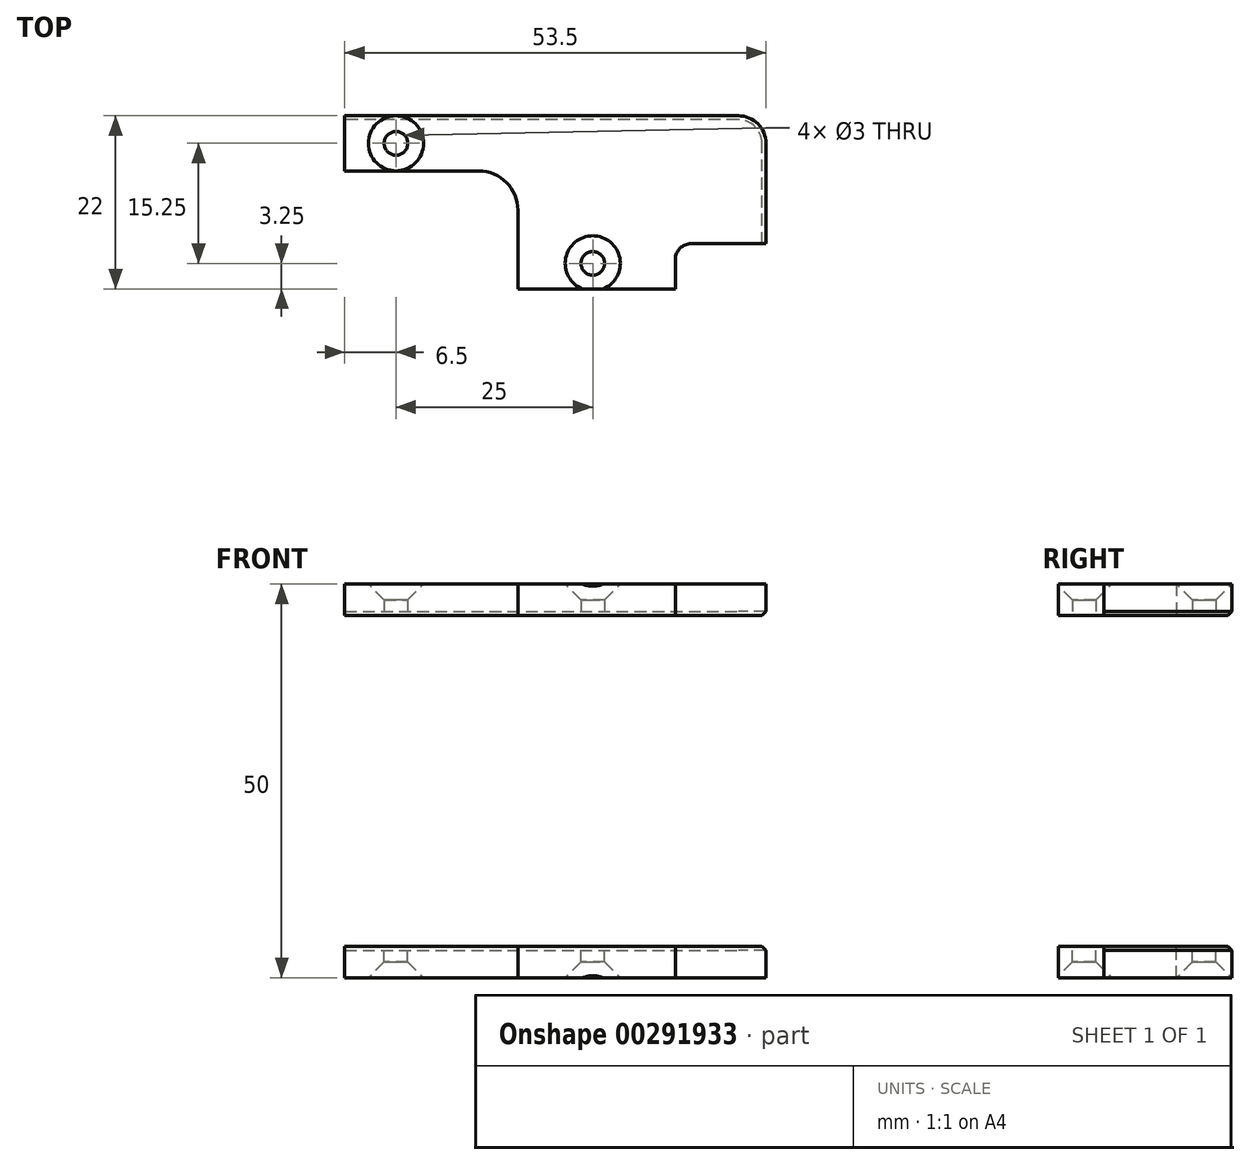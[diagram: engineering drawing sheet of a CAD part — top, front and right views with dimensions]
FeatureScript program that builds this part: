
annotation { "Feature Type Name" : "Feature", "Feature Type Description" : "" }
export const myFeature = defineFeature(function(context is Context, id is Id, definition is map)
    precondition{}
    {
        {
            var Q0;
            Q0=qCreatedBy(makeId("Top.planeOp"),FACE);
            var sketch = newSketch(context, id + "F0", { "sketchPlane" : qUnion([Q0])});
            skLineSegment(sketch, "E0.bottom", {"start": v(0, 0) * mm, "end": v(42, 0) * mm});
            skLineSegment(sketch, "E0.top", {"start": v(0, -22) * mm, "end": v(42, -22) * mm});
            skLineSegment(sketch, "E0.left", {"start": v(0, 0) * mm, "end": v(0, -22) * mm});
            skLineSegment(sketch, "E0.right", {"start": v(42, 0) * mm, "end": v(42, -22) * mm});
            skSolve(sketch);
        }
        {
            var Q0;
            Q0=makeQuery(id+"F0.imprint","IMPRINT",FACE,{"disambiguationData":[TD([[makeQuery(id+"F0.imprint","IMPRINT",EDGE,{"derivedFrom":sQuery(id+"F0.wireOp",EDGE,"E0.bottom")}),-1.0]])]});
            extrude(context, id + "F1", {"entities" : qUnion([Q0]), "depth" : 4 * mm});
        }
        {
            var Q0;
            Q0=qCreatedBy(makeId("Top.planeOp"),FACE);
            var sketch = newSketch(context, id + "F2", { "sketchPlane" : qUnion([Q0])});
            skLineSegment(sketch, "E1.bottom", {"start": v(24.5, 0) * mm, "end": v(53.5, 0) * mm});
            skLineSegment(sketch, "E1.top", {"start": v(24.5, -16.25) * mm, "end": v(53.5, -16.25) * mm});
            skLineSegment(sketch, "E1.left", {"start": v(24.5, 0) * mm, "end": v(24.5, -16.25) * mm});
            skLineSegment(sketch, "E1.right", {"start": v(53.5, 0) * mm, "end": v(53.5, -16.25) * mm});
            skSolve(sketch);
        }
        {
            var Q0;
            Q0=makeQuery(id+"F2.imprint","IMPRINT",FACE,{"disambiguationData":[TD([[makeQuery(id+"F2.imprint","IMPRINT",EDGE,{"derivedFrom":sQuery(id+"F2.wireOp",EDGE,"E1.bottom")}),-1.0]])]});
            extrude(context, id + "F3", {"entities" : qUnion([Q0]), "operationType" : NewBodyOperationType.ADD, "depth" : 4 * mm});
        }
        {
            var Q0;
            Q0=makeQuery(id+"F3.opExtrude","SWEPT_EDGE",EDGE,{"disambiguationData":[OSD([sQuery(id+"F2.wireOp",EDGE,"E1.bottom"),sQuery(id+"F2.wireOp",EDGE,"E1.right")])]});
            fillet(context, id + "F4", {"entities" : qUnion([Q0]), "radius" : 3.5 * mm, "tangentPropagation" : true, "allowEdgeOverflow" : false});
        }
        {
            var Q0;
            Q0=makeQuery(id+"F3.boolean.opBoolean","INTERSECT",EDGE,{"derivedFrom":[makeQuery(id+"F1.opExtrude","SWEPT_FACE",FACE,{"disambiguationData":[OSD([sQuery(id+"F0.wireOp",EDGE,"E0.right")])]}),makeQuery(id+"F3.opExtrude","SWEPT_FACE",FACE,{"disambiguationData":[OSD([sQuery(id+"F2.wireOp",EDGE,"E1.top")])]})]});
            fillet(context, id + "F5", {"entities" : qUnion([Q0]), "radius" : 2 * mm, "tangentPropagation" : true, "allowEdgeOverflow" : false});
        }
        {
            var Q0;
            Q0=makeQuery(id+"F3.boolean.opBoolean","MERGE",FACE,{"derivedFrom":[makeQuery(id+"F1.opExtrude","CAP_FACE",FACE,{"disambiguationData":[OSD([sQuery(id+"F0.wireOp",EDGE,"E0.bottom"),sQuery(id+"F0.wireOp",EDGE,"E0.top"),sQuery(id+"F0.wireOp",EDGE,"E0.left"),sQuery(id+"F0.wireOp",EDGE,"E0.right")])],"isStart":false}),makeQuery(id+"F3.opExtrude","CAP_FACE",FACE,{"disambiguationData":[OSD([sQuery(id+"F2.wireOp",EDGE,"E1.bottom"),sQuery(id+"F2.wireOp",EDGE,"E1.top"),sQuery(id+"F2.wireOp",EDGE,"E1.left"),sQuery(id+"F2.wireOp",EDGE,"E1.right")])],"isStart":false})]});
            var sketch = newSketch(context, id + "F6", { "sketchPlane" : qUnion([Q0])});
            skCircle(sketch, "E2", {"center": v(6.5, -3.5) * mm, "radius": 1.5 * mm});
            skSolve(sketch);
        }
        {
            var Q0;
            Q0=makeQuery(id+"F6.imprint","IMPRINT",FACE,{"disambiguationData":[TD([[makeQuery(id+"F6.imprint","IMPRINT",EDGE,{"derivedFrom":sQuery(id+"F6.wireOp",EDGE,"E2")}),1.0]])]});
            extrude(context, id + "F7", {"entities" : qUnion([Q0]), "operationType" : NewBodyOperationType.REMOVE, "oppositeDirection" : true, "depth" : 25 * mm});
        }
        {
            var Q0;
            Q0=makeQuery(id+"F3.boolean.opBoolean","MERGE",FACE,{"derivedFrom":[makeQuery(id+"F1.opExtrude","CAP_FACE",FACE,{"disambiguationData":[OSD([sQuery(id+"F0.wireOp",EDGE,"E0.bottom"),sQuery(id+"F0.wireOp",EDGE,"E0.top"),sQuery(id+"F0.wireOp",EDGE,"E0.left"),sQuery(id+"F0.wireOp",EDGE,"E0.right")])],"isStart":false}),makeQuery(id+"F3.opExtrude","CAP_FACE",FACE,{"disambiguationData":[OSD([sQuery(id+"F2.wireOp",EDGE,"E1.bottom"),sQuery(id+"F2.wireOp",EDGE,"E1.top"),sQuery(id+"F2.wireOp",EDGE,"E1.left"),sQuery(id+"F2.wireOp",EDGE,"E1.right")])],"isStart":false})]});
            var sketch = newSketch(context, id + "F8", { "sketchPlane" : qUnion([Q0])});
            skLineSegment(sketch, "E3.bottom", {"start": v(0, -22) * mm, "end": v(22, -22) * mm});
            skLineSegment(sketch, "E3.top", {"start": v(0, -7) * mm, "end": v(22, -7) * mm});
            skLineSegment(sketch, "E3.left", {"start": v(0, -22) * mm, "end": v(0, -7) * mm});
            skLineSegment(sketch, "E3.right", {"start": v(22, -22) * mm, "end": v(22, -7) * mm});
            skSolve(sketch);
        }
        {
            var Q0;
            Q0=makeQuery(id+"F8.imprint","IMPRINT",FACE,{"disambiguationData":[TD([[makeQuery(id+"F8.imprint","IMPRINT",EDGE,{"derivedFrom":sQuery(id+"F8.wireOp",EDGE,"E3.bottom")}),1.0]])]});
            extrude(context, id + "F9", {"entities" : qUnion([Q0]), "operationType" : NewBodyOperationType.REMOVE, "oppositeDirection" : true, "depth" : 25 * mm});
        }
        {
            var Q0;
            Q0=makeQuery(id+"F9.boolean.opBoolean","COPY",EDGE,{"derivedFrom":makeQuery(id+"F9.opExtrude","SWEPT_EDGE",EDGE,{"disambiguationData":[OSD([sQuery(id+"F8.wireOp",EDGE,"E3.top"),sQuery(id+"F8.wireOp",EDGE,"E3.right")])]})});
            fillet(context, id + "F10", {"entities" : qUnion([Q0]), "radius" : 5 * mm, "tangentPropagation" : true, "allowEdgeOverflow" : false});
        }
        {
            var Q0;
            Q0=makeQuery(id+"F3.boolean.opBoolean","MERGE",FACE,{"derivedFrom":[makeQuery(id+"F1.opExtrude","CAP_FACE",FACE,{"disambiguationData":[OSD([sQuery(id+"F0.wireOp",EDGE,"E0.bottom"),sQuery(id+"F0.wireOp",EDGE,"E0.top"),sQuery(id+"F0.wireOp",EDGE,"E0.left"),sQuery(id+"F0.wireOp",EDGE,"E0.right")])],"isStart":false}),makeQuery(id+"F3.opExtrude","CAP_FACE",FACE,{"disambiguationData":[OSD([sQuery(id+"F2.wireOp",EDGE,"E1.bottom"),sQuery(id+"F2.wireOp",EDGE,"E1.top"),sQuery(id+"F2.wireOp",EDGE,"E1.left"),sQuery(id+"F2.wireOp",EDGE,"E1.right")])],"isStart":false})]});
            var sketch = newSketch(context, id + "F11", { "sketchPlane" : qUnion([Q0])});
            skCircle(sketch, "E4", {"center": v(31.5, -18.75) * mm, "radius": 1.5 * mm});
            skSolve(sketch);
        }
        {
            var Q0;
            Q0=qSketchRegion(id+"F11",true);
            var Q1;
            Q1=sQuery(id+"F11.wireOp",EDGE,"E4");
            extrude(context, id + "F12", {"entities" : qUnion([Q0]), "operationType" : NewBodyOperationType.REMOVE, "surfaceEntities" : qUnion([Q1]), "oppositeDirection" : true, "depth" : 25 * mm});
        }
        {
            var Q0;
            Q0=qCreatedBy(makeId("Top.planeOp"),FACE);
            cPlane(context, id + "F13", {"entities" : qUnion([Q0]), "cplaneType" : CPlaneType.OFFSET, "offset" : 25 * mm, "width" : 150 * mm, "height" : 150 * mm});
        }
        {
            var Q0;
            Q0=makeQuery(id+"F12.boolean.opBoolean","INTERSECT",EDGE,{"derivedFrom":[makeQuery(id+"F3.boolean.opBoolean","MERGE",FACE,{"derivedFrom":[makeQuery(id+"F1.opExtrude","CAP_FACE",FACE,{"disambiguationData":[OSD([sQuery(id+"F0.wireOp",EDGE,"E0.bottom"),sQuery(id+"F0.wireOp",EDGE,"E0.top"),sQuery(id+"F0.wireOp",EDGE,"E0.left"),sQuery(id+"F0.wireOp",EDGE,"E0.right")])],"isStart":true}),makeQuery(id+"F3.opExtrude","CAP_FACE",FACE,{"disambiguationData":[OSD([sQuery(id+"F2.wireOp",EDGE,"E1.bottom"),sQuery(id+"F2.wireOp",EDGE,"E1.top"),sQuery(id+"F2.wireOp",EDGE,"E1.left"),sQuery(id+"F2.wireOp",EDGE,"E1.right")])],"isStart":true})]}),makeQuery(id+"F12.opExtrude","SWEPT_FACE",FACE,{"disambiguationData":[OSD([sQuery(id+"F11.wireOp",EDGE,"E4")])]})]});
            var Q1;
            Q1=makeQuery(id+"F7.boolean.opBoolean","INTERSECT",EDGE,{"derivedFrom":[makeQuery(id+"F3.boolean.opBoolean","MERGE",FACE,{"derivedFrom":[makeQuery(id+"F1.opExtrude","CAP_FACE",FACE,{"disambiguationData":[OSD([sQuery(id+"F0.wireOp",EDGE,"E0.bottom"),sQuery(id+"F0.wireOp",EDGE,"E0.top"),sQuery(id+"F0.wireOp",EDGE,"E0.left"),sQuery(id+"F0.wireOp",EDGE,"E0.right")])],"isStart":true}),makeQuery(id+"F3.opExtrude","CAP_FACE",FACE,{"disambiguationData":[OSD([sQuery(id+"F2.wireOp",EDGE,"E1.bottom"),sQuery(id+"F2.wireOp",EDGE,"E1.top"),sQuery(id+"F2.wireOp",EDGE,"E1.left"),sQuery(id+"F2.wireOp",EDGE,"E1.right")])],"isStart":true})]}),makeQuery(id+"F7.opExtrude","SWEPT_FACE",FACE,{"disambiguationData":[OSD([sQuery(id+"F6.wireOp",EDGE,"E2")])]})]});
            chamfer(context, id + "F14", {"entities" : qUnion([Q0, Q1]), "width" : 2 * mm, "tangentPropagation" : true});
        }
        {
            var Q0;
            Q0=makeQuery(id+"F3.opExtrude","CAP_EDGE",EDGE,{"disambiguationData":[OSD([sQuery(id+"F2.wireOp",EDGE,"E1.right")])],"isStart":false});
            var Q1;
            {var subQ0=sQuery(id+"F2.wireOp",EDGE,"E1.right");var subQ1=sQuery(id+"F2.wireOp",EDGE,"E1.bottom");Q1=makeQuery(id+"F4.opFillet","BLEND_EDGE",EDGE,{"blendedFrom":[makeQuery(id+"F3.opExtrude","SWEPT_EDGE",EDGE,{"disambiguationData":[OSD([subQ1,subQ0])]}),makeQuery(id+"F3.boolean.opBoolean","MERGE",FACE,{"derivedFrom":[makeQuery(id+"F1.opExtrude","CAP_FACE",FACE,{"disambiguationData":[OSD([sQuery(id+"F0.wireOp",EDGE,"E0.bottom"),sQuery(id+"F0.wireOp",EDGE,"E0.top"),sQuery(id+"F0.wireOp",EDGE,"E0.left"),sQuery(id+"F0.wireOp",EDGE,"E0.right")])],"isStart":false}),makeQuery(id+"F3.opExtrude","CAP_FACE",FACE,{"disambiguationData":[OSD([subQ1,sQuery(id+"F2.wireOp",EDGE,"E1.top"),sQuery(id+"F2.wireOp",EDGE,"E1.left"),subQ0])],"isStart":false})]})],"blendedInto":[makeQuery(id+"F3.boolean.opBoolean","MERGE",FACE,{"derivedFrom":[makeQuery(id+"F1.opExtrude","CAP_FACE",FACE,{"disambiguationData":[OSD([sQuery(id+"F0.wireOp",EDGE,"E0.bottom"),sQuery(id+"F0.wireOp",EDGE,"E0.top"),sQuery(id+"F0.wireOp",EDGE,"E0.left"),sQuery(id+"F0.wireOp",EDGE,"E0.right")])],"isStart":false}),makeQuery(id+"F3.opExtrude","CAP_FACE",FACE,{"disambiguationData":[OSD([subQ1,sQuery(id+"F2.wireOp",EDGE,"E1.top"),sQuery(id+"F2.wireOp",EDGE,"E1.left"),subQ0])],"isStart":false})]})]});}
            var Q2;
            Q2=makeQuery(id+"F3.boolean.opBoolean","MERGE",EDGE,{"derivedFrom":[makeQuery(id+"F1.opExtrude","CAP_EDGE",EDGE,{"disambiguationData":[OSD([sQuery(id+"F0.wireOp",EDGE,"E0.bottom")])],"isStart":false}),makeQuery(id+"F3.opExtrude","CAP_EDGE",EDGE,{"disambiguationData":[OSD([sQuery(id+"F2.wireOp",EDGE,"E1.bottom")])],"isStart":false})]});
            chamfer(context, id + "F15", {"entities" : qUnion([Q0, Q1, Q2]), "width" : 0.5 * mm, "tangentPropagation" : true});
        }
        {
            var Q0;
            Q0=makeQuery(id+"F1.opExtrude","SWEPT_BODY",BODY,{"disambiguationData":[OSD([sQuery(id+"F0.wireOp",EDGE,"E0.bottom"),sQuery(id+"F0.wireOp",EDGE,"E0.top"),sQuery(id+"F0.wireOp",EDGE,"E0.left"),sQuery(id+"F0.wireOp",EDGE,"E0.right")])]});
            var Q1;
            Q1=qCreatedBy(id+"F13.planeOp",FACE);
            mirror(context, id + "F16", {"entities" : qUnion([Q0]), "mirrorPlane" : qUnion([Q1])});
        }
    });
